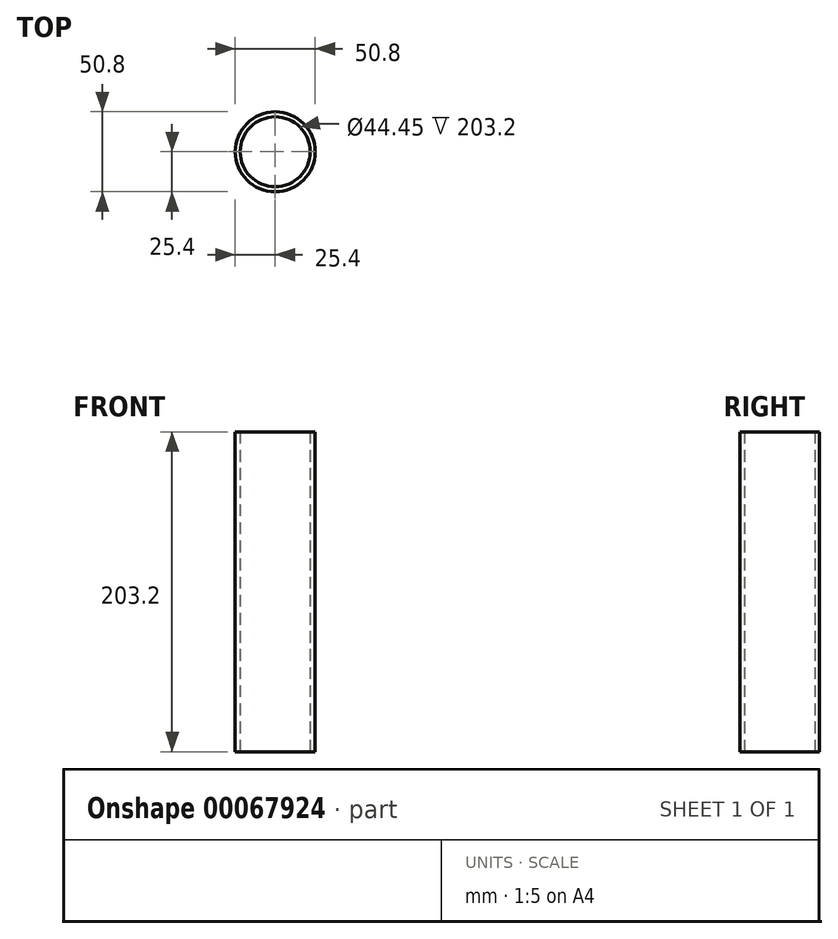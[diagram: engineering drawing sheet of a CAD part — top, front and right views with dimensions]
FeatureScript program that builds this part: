
annotation { "Feature Type Name" : "Feature", "Feature Type Description" : "" }
export const myFeature = defineFeature(function(context is Context, id is Id, definition is map)
    precondition{}
    {
        {
            var Q0;
            Q0=qCreatedBy(makeId("Top.planeOp"),FACE);
            var sketch = newSketch(context, id + "F0", { "sketchPlane" : qUnion([Q0])});
            skCircle(sketch, "E0", {"center": v(0, 0) * mm, "radius": 25.4 * mm});
            skCircle(sketch, "E1", {"center": v(0, 0) * mm, "radius": 22.23 * mm});
            skSolve(sketch);
        }
        {
            var Q0;
            Q0=makeQuery(id+"F0.imprint","IMPRINT",FACE,{"disambiguationData":[TD([[makeQuery(id+"F0.imprint","IMPRINT",EDGE,{"derivedFrom":sQuery(id+"F0.wireOp",EDGE,"E0")}),1.0]])]});
            extrude(context, id + "F1", {"entities" : qUnion([Q0]), "depth" : 203.2 * mm});
        }
    });
